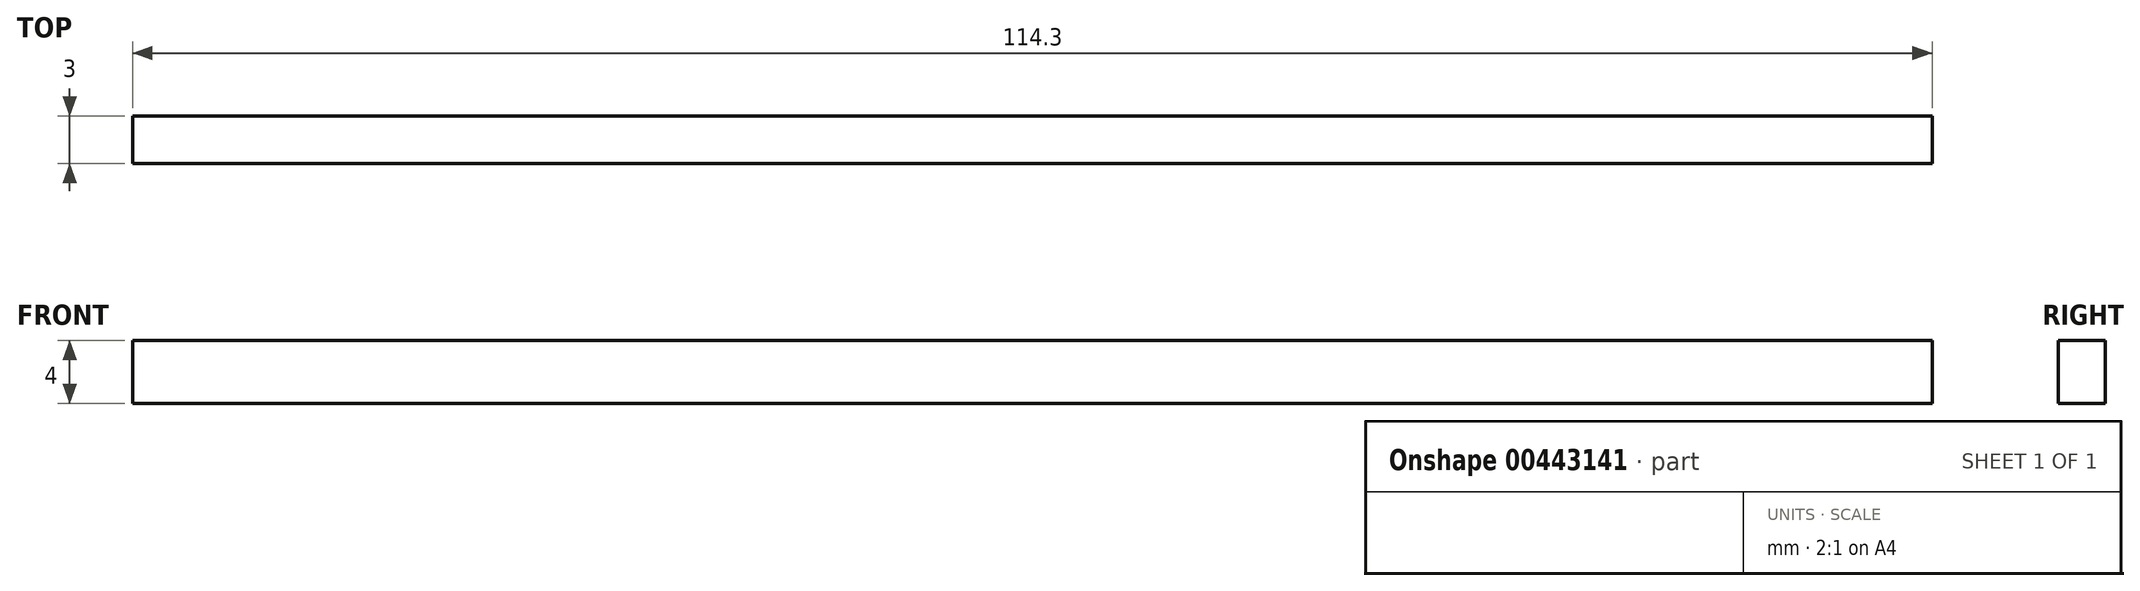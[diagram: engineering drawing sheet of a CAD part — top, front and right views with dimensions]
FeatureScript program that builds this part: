
annotation { "Feature Type Name" : "Feature", "Feature Type Description" : "" }
export const myFeature = defineFeature(function(context is Context, id is Id, definition is map)
    precondition{}
    {
        {
            var Q0;
            Q0=qCreatedBy(makeId("Front.planeOp"),FACE);
            var sketch = newSketch(context, id + "F0", { "sketchPlane" : qUnion([Q0])});
            skLineSegment(sketch, "E0.bottom", {"start": v(-102.63, 24.54) * mm, "end": v(11.67, 24.54) * mm});
            skLineSegment(sketch, "E0.top", {"start": v(-102.63, 28.54) * mm, "end": v(11.67, 28.54) * mm});
            skLineSegment(sketch, "E0.left", {"start": v(-102.63, 24.54) * mm, "end": v(-102.63, 28.54) * mm});
            skLineSegment(sketch, "E0.right", {"start": v(11.67, 24.54) * mm, "end": v(11.67, 28.54) * mm});
            skSolve(sketch);
        }
        {
            var Q0;
            Q0=makeQuery(id+"F0.imprint","IMPRINT",FACE,{"disambiguationData":[TD([[makeQuery(id+"F0.imprint","IMPRINT",EDGE,{"derivedFrom":sQuery(id+"F0.wireOp",EDGE,"E0.bottom")}),1.0]])]});
            extrude(context, id + "F1", {"entities" : qUnion([Q0]), "depth" : 3 * mm});
        }
    });
